# Revit family: KS ALU-PU 80, DS 50, o.Blz, M10-M12, Ø 17,2-168,3
name_source: partatom
category: HLS-Bauteile
units: mm (PartAtom-declared; Revit-internal decimal feet)

## family parameters
Arbeitsebenenbasiert = Ja
Beim Laden mit Abzugskörper schneiden = Nein
Bemaßung runder Anschluss = Durchmesser verwenden
Beschriftungsausrichtung beibehalten = Nein
Gemeinsam genutzt = Ja
Immer vertikal = Nein
Raumberechnungspunkt = Nein
Teiletyp = Normal

## types (19) — shared parameters
Anschluss = M10/M12
Baustoffklasse = B2
DS = 50 mm  [stored 0.164042 ft]
DVS = 18 mm  [stored 0.0590551 ft]
Dichte Kern = 80 kg/m³
Dichte Mantel = 2700 kg/m³
Dicke Mantel = 0.08 mm
Dämmkörper = ALU/PU
Dämmstärke = 50 mm  [stored 0.164042 ft]
Fabrikat = MEFA
Firma = MEFA Befestigungs- und Montagesysteme GmbH
HGA = 22 mm  [stored 0.0721785 ft]
Kurztext1 = Kälteschelle RG80 ALU/PU
L = 100 mm
Material = Stahl
Material Mantel = Alufolie
Materialname = S235
Mengeneinheit = St
Oberflaeche = galvanisch verzinkt
Rohrschellentyp = Maxima PSM
Schalenlänge = 100 mm
Vorgabe-Ansicht = 1219 mm
Wasserdampfdiffusionswiderstand = 18750 µ
Wärmeleitfähigkeit = 0.025 W/mK
max. Temperaturbeständigkeit = 120 °C
mittl. Nenndruckfestigkeit Kern = 0.5 N/mm²
stat. Belastung Kern = 0.1 N/mm²
vpe = 1

## per-type parameters (varying)
- Kälteschelle ALU-PU 80, DS 50, o.Blz, M10/M12, Ø 17,2: A=75 mm; AB=2 mm  [stored 0.00656168 ft]; Anschlußhöhe=76 mm; Artikelnummer=76501742; B=184 mm; Breite=184 mm; D=18 mm  [stored 0.0590551 ft]; D0=118 mm; DF1=29 mm  [stored 0.0951444 ft]; DF2=29 mm  [stored 0.0951444 ft]; Dmax=20 mm  [stored 0.0656168 ft]; Dmin=16 mm  [stored 0.0524934 ft]; EAN=4250928444950; Gewicht=0.52 kg; Gewicht pro Bauteil=0.52 kg; H=146 mm; Kurztext2=17,2 mm Iso 50 x 100 mm M10/M12; MB=30 mm  [stored 0.0984252 ft]; MD=3 mm  [stored 0.00984252 ft]; R=59 mm; RM=62 mm  [stored 0.203412 ft]; Rohraußendurchmesser Kupfer=18 mm; Rohraußendurchmesser Stahl=17,2 mm; S=155 mm; max. zul. Last=0.30 kN
- Kälteschelle ALU-PU 80, DS 50, o.Blz, M10/M12, Ø 21,3: A=75 mm; AB=2 mm  [stored 0.00656168 ft]; Anschlußhöhe=75 mm; Artikelnummer=76502142; B=184 mm; Breite=184 mm; D=22 mm  [stored 0.0721785 ft]; D0=122 mm; DF1=27 mm  [stored 0.0885827 ft]; DF2=27 mm  [stored 0.0885827 ft]; Dmax=24 mm  [stored 0.0787402 ft]; Dmin=20 mm  [stored 0.0656168 ft]; EAN=4250928444974; Gewicht=0.52 kg; Gewicht pro Bauteil=0.52 kg; H=150 mm; Kurztext2=21,3 mm Iso 50 x 100 mm M10/M12; MB=30 mm  [stored 0.0984252 ft]; MD=3 mm  [stored 0.00984252 ft]; R=61 mm  [stored 0.200131 ft]; RM=64 mm  [stored 0.209974 ft]; Rohraußendurchmesser Kupfer=22 mm; Rohraußendurchmesser Stahl=21,3 mm; S=157 mm; max. zul. Last=0.30 kN
- Kälteschelle ALU-PU 80, DS 50, o.Blz, M10/M12, Ø 26,9: A=75 mm; AB=3 mm  [stored 0.00984252 ft]; Anschlußhöhe=74 mm; Artikelnummer=76502742; B=189 mm; Breite=189 mm; D=28 mm  [stored 0.0918635 ft]; D0=128 mm; DF1=27 mm  [stored 0.0885827 ft]; DF2=26 mm; Dmax=30 mm  [stored 0.0984252 ft]; Dmin=25 mm  [stored 0.082021 ft]; EAN=4250928444998; Gewicht=0.54 kg; Gewicht pro Bauteil=0.54 kg; H=156 mm; Kurztext2=26,9 mm Iso 50 x 100 mm M10/M12; MB=30 mm  [stored 0.0984252 ft]; MD=3 mm  [stored 0.00984252 ft]; R=64 mm  [stored 0.209974 ft]; RM=67 mm; Rohraußendurchmesser Kupfer=28 mm; Rohraußendurchmesser Stahl=26,9 mm; S=162 mm; max. zul. Last=0.40 kN
- Kälteschelle ALU-PU 80, DS 50, o.Blz, M10/M12, Ø 33,7: A=76 mm; AB=3 mm  [stored 0.00984252 ft]; Anschlußhöhe=76 mm; Artikelnummer=76503444; B=210 mm; Breite=209 mm; D=35 mm  [stored 0.114829 ft]; D0=135 mm; DF1=33 mm  [stored 0.108268 ft]; DF2=33 mm  [stored 0.108268 ft]; Dmax=36 mm  [stored 0.11811 ft]; Dmin=32 mm  [stored 0.104987 ft]; EAN=4250928445018; Gewicht=0.82 kg; Gewicht pro Bauteil=0.82 kg; H=165 mm; Kurztext2=33,7 mm Iso 50 x 100 mm M10/M12; MB=35 mm  [stored 0.114829 ft]; MD=4 mm  [stored 0.0131234 ft]; R=68 mm; RM=72 mm; Rohraußendurchmesser Kupfer=35 mm; Rohraußendurchmesser Stahl=33,7 mm; S=177 mm; max. zul. Last=0.50 kN
- Kälteschelle ALU-PU 80, DS 50, o.Blz, M10/M12, Ø 42,4: A=76 mm; AB=2 mm  [stored 0.00656168 ft]; Anschlußhöhe=75 mm; Artikelnummer=76504244; B=217 mm; Breite=216 mm; D=42 mm; D0=142 mm; DF1=32 mm  [stored 0.104987 ft]; DF2=33 mm  [stored 0.108268 ft]; Dmax=44 mm  [stored 0.144357 ft]; Dmin=40 mm  [stored 0.131234 ft]; EAN=4250928445032; Gewicht=0.85 kg; Gewicht pro Bauteil=0.85 kg; H=172 mm; Kurztext2=42,4 mm Iso 50 x 100 mm M10/M12; MB=35 mm  [stored 0.114829 ft]; MD=4 mm  [stored 0.0131234 ft]; R=71 mm; RM=75 mm; Rohraußendurchmesser Kupfer=42 mm; Rohraußendurchmesser Stahl=42,4 mm; S=185 mm; max. zul. Last=0.60 kN
- Kälteschelle ALU-PU 80, DS 50, o.Blz, M10/M12, Ø 48,3: A=76 mm; AB=2 mm  [stored 0.00656168 ft]; Anschlußhöhe=76 mm; Artikelnummer=76504844; B=227 mm; Breite=226 mm; D=48 mm; D0=148 mm; DF1=33 mm  [stored 0.108268 ft]; DF2=34 mm; Dmax=52 mm; Dmin=46 mm  [stored 0.150919 ft]; EAN=4250928445056; Gewicht=0.90 kg; Gewicht pro Bauteil=0.90 kg; H=178 mm; Kurztext2=48,3 mm Iso 50 x 100 mm M10/M12; MB=35 mm  [stored 0.114829 ft]; MD=4 mm  [stored 0.0131234 ft]; R=74 mm; RM=78 mm; Rohraußendurchmesser Stahl=48,3 mm; S=194 mm; max. zul. Last=0.70 kN
- Kälteschelle ALU-PU 80, DS 50, o.Blz, M10/M12, Ø 54: A=76 mm; AB=4 mm  [stored 0.0131234 ft]; Anschlußhöhe=75 mm; Artikelnummer=76505444; B=235 mm; Breite=234 mm; D=54 mm  [stored 0.177165 ft]; D0=154 mm; DF1=34 mm; DF2=35 mm  [stored 0.114829 ft]; Dmax=58 mm  [stored 0.190289 ft]; Dmin=50 mm  [stored 0.164042 ft]; EAN=4250928445070; Gewicht=0.94 kg; Gewicht pro Bauteil=0.94 kg; H=184 mm; Kurztext2=54 mm Iso 50 x 100 mm M10/M12; MB=35 mm  [stored 0.114829 ft]; MD=4 mm  [stored 0.0131234 ft]; R=77 mm; RM=81 mm; Rohraußendurchmesser Kupfer=54 mm; S=201 mm; max. zul. Last=0.70 kN
- Kälteschelle ALU-PU 80, DS 50, o.Blz, M10/M12, Ø 57: A=76 mm; AB=2 mm  [stored 0.00656168 ft]; Anschlußhöhe=76 mm; Artikelnummer=76505744; B=235 mm; Breite=234 mm; D=57 mm  [stored 0.187008 ft]; D0=157 mm; DF1=34 mm; DF2=33 mm  [stored 0.108268 ft]; Dmax=60 mm  [stored 0.19685 ft]; Dmin=55 mm  [stored 0.180446 ft]; EAN=4250928445094; Gewicht=0.93 kg; Gewicht pro Bauteil=0.93 kg; H=187 mm; Kurztext2=57 mm Iso 50 x 100 mm M10/M12; MB=35 mm  [stored 0.114829 ft]; MD=4 mm  [stored 0.0131234 ft]; R=79 mm; RM=83 mm; Rohraußendurchmesser Stahl=57 mm; S=201 mm; max. zul. Last=0.80 kN
- Kälteschelle ALU-PU 80, DS 50, o.Blz, M10/M12, Ø 60,3: A=76 mm; AB=2 mm  [stored 0.00656168 ft]; Anschlußhöhe=75 mm; Artikelnummer=76506044; B=235 mm; Breite=234 mm; D=60 mm  [stored 0.19685 ft]; D0=160 mm; DF1=33 mm  [stored 0.108268 ft]; DF2=32 mm  [stored 0.104987 ft]; Dmax=62 mm  [stored 0.203412 ft]; Dmin=58 mm  [stored 0.190289 ft]; EAN=4250928445117; Gewicht=0.94 kg; Gewicht pro Bauteil=0.94 kg; H=190 mm; Kurztext2=60,3 mm Iso 50 x 100 mm M10/M12; MB=35 mm  [stored 0.114829 ft]; MD=4 mm  [stored 0.0131234 ft]; R=80 mm; RM=84 mm; Rohraußendurchmesser Stahl=60,3 mm; S=202 mm; max. zul. Last=0.80 kN
- Kälteschelle ALU-PU 80, DS 50, o.Blz, M10/M12, Ø 63,5: A=76 mm; AB=3 mm  [stored 0.00984252 ft]; Anschlußhöhe=76 mm; Artikelnummer=76506444; B=242 mm; Breite=240 mm; D=64 mm  [stored 0.209974 ft]; D0=164 mm; DF1=35 mm  [stored 0.114829 ft]; DF2=34 mm; Dmax=65 mm  [stored 0.213255 ft]; Dmin=61 mm  [stored 0.200131 ft]; EAN=4250928445131; Gewicht=0.97 kg; Gewicht pro Bauteil=0.97 kg; H=194 mm; Kurztext2=63,5 mm Iso 50 x 100 mm M10/M12; MB=35 mm  [stored 0.114829 ft]; MD=4 mm  [stored 0.0131234 ft]; R=82 mm; RM=86 mm; Rohraußendurchmesser Stahl=63,5 mm; S=207 mm; max. zul. Last=0.80 kN
- Kälteschelle ALU-PU 80, DS 50, o.Blz, M10/M12, Ø 76,1: A=76 mm; AB=2 mm  [stored 0.00656168 ft]; Anschlußhöhe=76 mm; Artikelnummer=76507644; B=253 mm; Breite=252 mm; D=76 mm; D0=176 mm; DF1=33 mm  [stored 0.108268 ft]; DF2=34 mm; Dmax=78 mm; Dmin=74 mm; EAN=4250928445179; Gewicht=1.03 kg; Gewicht pro Bauteil=1.03 kg; H=206 mm; Kurztext2=76,1 mm Iso 50 x 100 mm M10/M12; MB=35 mm  [stored 0.114829 ft]; MD=4 mm  [stored 0.0131234 ft]; R=88 mm; RM=92 mm; Rohraußendurchmesser Stahl=76,1 mm; S=220 mm; max. zul. Last=0.90 kN
- Kälteschelle ALU-PU 80, DS 50, o.Blz, M10/M12, Ø 88,9: A=76 mm; AB=1 mm  [stored 0.00328084 ft]; Anschlußhöhe=76 mm; Artikelnummer=76508944; B=266 mm; Breite=265 mm; D=89 mm; D0=189 mm; DF1=34 mm; DF2=34 mm; Dmax=90 mm; Dmin=88 mm; EAN=4250928445193; Gewicht=1.09 kg; Gewicht pro Bauteil=1.09 kg; H=219 mm; Kurztext2=88,9 mm Iso 50 x 100 mm M10/M12; MB=35 mm  [stored 0.114829 ft]; MD=4 mm  [stored 0.0131234 ft]; R=94 mm; RM=98 mm; Rohraußendurchmesser Stahl=88,9 mm; S=232 mm; max. zul. Last=1.00 kN
- Kälteschelle ALU-PU 80, DS 50, o.Blz, M10/M12, Ø108: A=76 mm; AB=2 mm  [stored 0.00656168 ft]; Anschlußhöhe=77 mm; Artikelnummer=76510844; B=288 mm; Breite=297 mm; D=108 mm; D0=208 mm; DF1=35 mm  [stored 0.114829 ft]; DF2=35 mm  [stored 0.114829 ft]; Dmax=110 mm; Dmin=106 mm; EAN=4250928445216; Gewicht=1.19 kg; Gewicht pro Bauteil=1.19 kg; H=238 mm; Kurztext2=108 mm Iso 50 x 100 mm M10/M12; MB=35 mm  [stored 0.114829 ft]; MD=4 mm  [stored 0.0131234 ft]; R=104 mm; RM=108 mm; Rohraußendurchmesser Stahl=108 mm; S=253 mm; max. zul. Last=1.10 kN
- Kälteschelle ALU-PU 80, DS 50, o.Blz, M10/M12, Ø114,3: A=76 mm; AB=2 mm  [stored 0.00656168 ft]; Anschlußhöhe=78 mm; Artikelnummer=7651146; B=298 mm; Breite=297 mm; D=114 mm; D0=214 mm; DF1=37 mm  [stored 0.121391 ft]; DF2=37 mm  [stored 0.121391 ft]; Dmax=116 mm; Dmin=112 mm; EAN=4250928445247; Gewicht=1.24 kg; Gewicht pro Bauteil=1.24 kg; H=244 mm; Kurztext2=114,3 mm Iso 50 x 100 mm M10/M12; MB=35 mm  [stored 0.114829 ft]; MD=4 mm  [stored 0.0131234 ft]; R=107 mm; RM=111 mm; Rohraußendurchmesser Stahl=114.3 mm; S=261 mm; max. zul. Last=1.10 kN
- Kälteschelle ALU-PU 80, DS 50, o.Blz, M10/M12, Ø133: A=76 mm; AB=1 mm  [stored 0.00328084 ft]; Anschlußhöhe=75 mm; Artikelnummer=76513344; B=308 mm; Breite=308 mm; D=133 mm; D0=233 mm; DF1=33 mm  [stored 0.108268 ft]; DF2=33 mm  [stored 0.108268 ft]; Dmax=134 mm; Dmin=132 mm; EAN=4250928445254; Gewicht=1.29 kg; Gewicht pro Bauteil=1.29 kg; H=263 mm; Kurztext2=133 mm Iso 50 x 100 mm M10/M12; MB=35 mm  [stored 0.114829 ft]; MD=4 mm  [stored 0.0131234 ft]; R=117 mm; RM=121 mm; Rohraußendurchmesser Stahl=133 mm; S=275 mm; max. zul. Last=1.20 kN
- Kälteschelle ALU-PU 80, DS 50, o.Blz, M10/M12, Ø139,7: A=76 mm; AB=2 mm  [stored 0.00656168 ft]; Anschlußhöhe=75 mm; Artikelnummer=76514044; B=315 mm; Breite=315 mm; D=140 mm; D0=240 mm; DF1=33 mm  [stored 0.108268 ft]; DF2=34 mm; Dmax=140 mm; Dmin=138 mm; EAN=4250928445285; Gewicht=1.32 kg; Gewicht pro Bauteil=1.32 kg; H=270 mm; Kurztext2=139,7 mm Iso 50 x 100 mm M10/M12; MB=35 mm  [stored 0.114829 ft]; MD=4 mm  [stored 0.0131234 ft]; R=120 mm; RM=124 mm; Rohraußendurchmesser Stahl=139,7 mm; S=282 mm; max. zul. Last=1.20 kN
- Kälteschelle ALU-PU 80, DS 50, o.Blz, M10/M12, Ø159: A=76 mm; AB=1 mm  [stored 0.00328084 ft]; Anschlußhöhe=77 mm; Artikelnummer=76515944; B=340 mm; Breite=340 mm; D=159 mm; D0=259 mm; DF1=36 mm  [stored 0.11811 ft]; DF2=36 mm  [stored 0.11811 ft]; Dmax=160 mm; Dmin=158 mm; EAN=4250928445315; Gewicht=1.45 kg; Gewicht pro Bauteil=1.45 kg; H=289 mm; Kurztext2=159 mm Iso 50 x 100 mm M10/M12; MB=35 mm  [stored 0.114829 ft]; MD=4 mm  [stored 0.0131234 ft]; R=130 mm; RM=134 mm; Rohraußendurchmesser Stahl=159 mm; S=304 mm; max. zul. Last=1.30 kN
- Kälteschelle ALU-PU 80, DS 50, o.Blz, M10/M12, Ø168,3: A=76 mm; AB=2 mm  [stored 0.00656168 ft]; Anschlußhöhe=76 mm; Artikelnummer=76516844; B=346 mm; Breite=346 mm; D=168 mm; D0=268 mm; DF1=34 mm; DF2=34 mm; Dmax=170 mm; Dmin=166 mm; EAN=4250928445346; Gewicht=1.48 kg; Gewicht pro Bauteil=1.48 kg; H=298 mm; Kurztext2=168,3 mm Iso 50 x 100 mm M10/M12; MB=35 mm  [stored 0.114829 ft]; MD=4 mm  [stored 0.0131234 ft]; R=134 mm; RM=138 mm; Rohraußendurchmesser Stahl=168,3 mm; S=312 mm; max. zul. Last=1.40 kN
- Kälteschelle ALU-PU 80, DS 50, o.Blz, M10/M12, Ø 70: A=76 mm; AB=2 mm  [stored 0.00656168 ft]; Anschlußhöhe=76 mm; Artikelnummer=76507044; B=248 mm; Breite=247 mm; D=70 mm; D0=170 mm; DF1=35 mm  [stored 0.114829 ft]; DF2=34 mm; Dmax=71 mm; Dmin=68 mm; EAN=4250928445155; Gewicht=1.00 kg; Gewicht pro Bauteil=1.00 kg; H=200 mm; Kurztext2=70 mm Iso 50 x 100 mm M10/M12; MB=35 mm  [stored 0.114829 ft]; MD=4 mm  [stored 0.0131234 ft]; R=85 mm; RM=89 mm; Rohraußendurchmesser Stahl=70 mm; S=213 mm; max. zul. Last=0.90 kN

note: [stored X ft] marks values corroborated as IEEE doubles in the binary element streams (Revit-internal decimal feet)

## geometry (parser evidence)
native form markers: Sweep x4
no freeform markers — native parametric forms only
